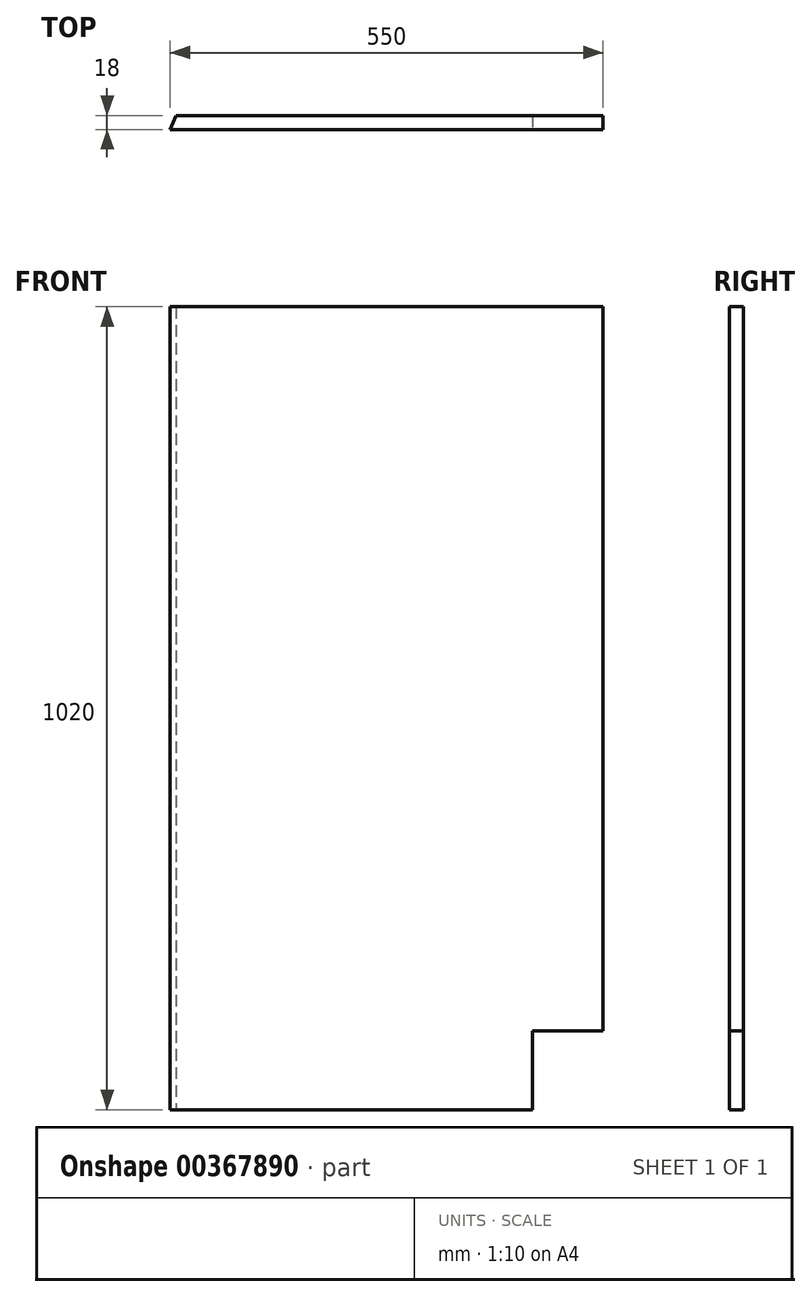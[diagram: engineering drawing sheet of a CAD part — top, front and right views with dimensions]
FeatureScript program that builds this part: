
annotation { "Feature Type Name" : "Feature", "Feature Type Description" : "" }
export const myFeature = defineFeature(function(context is Context, id is Id, definition is map)
    precondition{}
    {
        {
            var Q0;
            Q0=qCreatedBy(makeId("Top.planeOp"),FACE);
            var sketch = newSketch(context, id + "F0", { "sketchPlane" : qUnion([Q0])});
            skLineSegment(sketch, "E0", {"start": v(0, 0) * mm, "end": v(550, 0) * mm});
            skLineSegment(sketch, "E1", {"start": v(550, 0) * mm, "end": v(550, 18) * mm});
            skLineSegment(sketch, "E2", {"start": v(550, 18) * mm, "end": v(7.46, 18) * mm});
            skLineSegment(sketch, "E3", {"start": v(7.46, 18) * mm, "end": v(0, 0) * mm});
            skSolve(sketch);
        }
        {
            var Q0;
            Q0=makeQuery(id+"F0.imprint","IMPRINT",FACE,{"disambiguationData":[TD([[makeQuery(id+"F0.imprint","IMPRINT",EDGE,{"derivedFrom":sQuery(id+"F0.wireOp",EDGE,"E0")}),1.0]])]});
            extrude(context, id + "F1", {"entities" : qUnion([Q0]), "depth" : 1020 * mm});
        }
        {
            var Q0;
            Q0=qCreatedBy(makeId("Front.planeOp"),FACE);
            var sketch = newSketch(context, id + "F2", { "sketchPlane" : qUnion([Q0])});
            skLineSegment(sketch, "E4.bottom", {"start": v(550, 0) * mm, "end": v(460, 0) * mm});
            skLineSegment(sketch, "E4.top", {"start": v(550, 100) * mm, "end": v(460, 100) * mm});
            skLineSegment(sketch, "E4.left", {"start": v(550, 0) * mm, "end": v(550, 100) * mm});
            skLineSegment(sketch, "E4.right", {"start": v(460, 0) * mm, "end": v(460, 100) * mm});
            skSolve(sketch);
        }
        {
            var Q0;
            Q0=makeQuery(id+"F2.imprint","IMPRINT",FACE,{"disambiguationData":[TD([[makeQuery(id+"F2.imprint","IMPRINT",EDGE,{"derivedFrom":sQuery(id+"F2.wireOp",EDGE,"E4.bottom")}),-1.0]])]});
            extrude(context, id + "F3", {"entities" : qUnion([Q0]), "operationType" : NewBodyOperationType.REMOVE, "oppositeDirection" : true, "depth" : 25 * mm});
        }
    });
